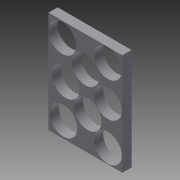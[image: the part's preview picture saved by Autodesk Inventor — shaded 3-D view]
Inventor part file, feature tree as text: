
AUTODESK INVENTOR PART (.ipt)
format: ipt  version: 2015 (Build 190159000, 159)  size: 118,272 bytes
history: native  units: in
note: dims shown in document units (in); Inventor stores cm internally (conversion verified against a paired STEP export)
features: extrude x1, sketch x1
ambient origin geometry x8: Origin, YZ Plane, XZ Plane, XY Plane, X Axis, Y Axis, Z Axis, Center Point
bodies: Solid1 (feature_tree)
feature tree (2):
  extrude  "Extrusion1"  Depth=11.0in
  sketch  "Sketch1"  dims[d0=8.0in d1=11.0in d2=3.0in d3=3.0in d4=3.0in d5=3.0in d6=3.0in d7=3.0in d8=3.0in d9=3.0in d10=1.0in d11=0.0in]
